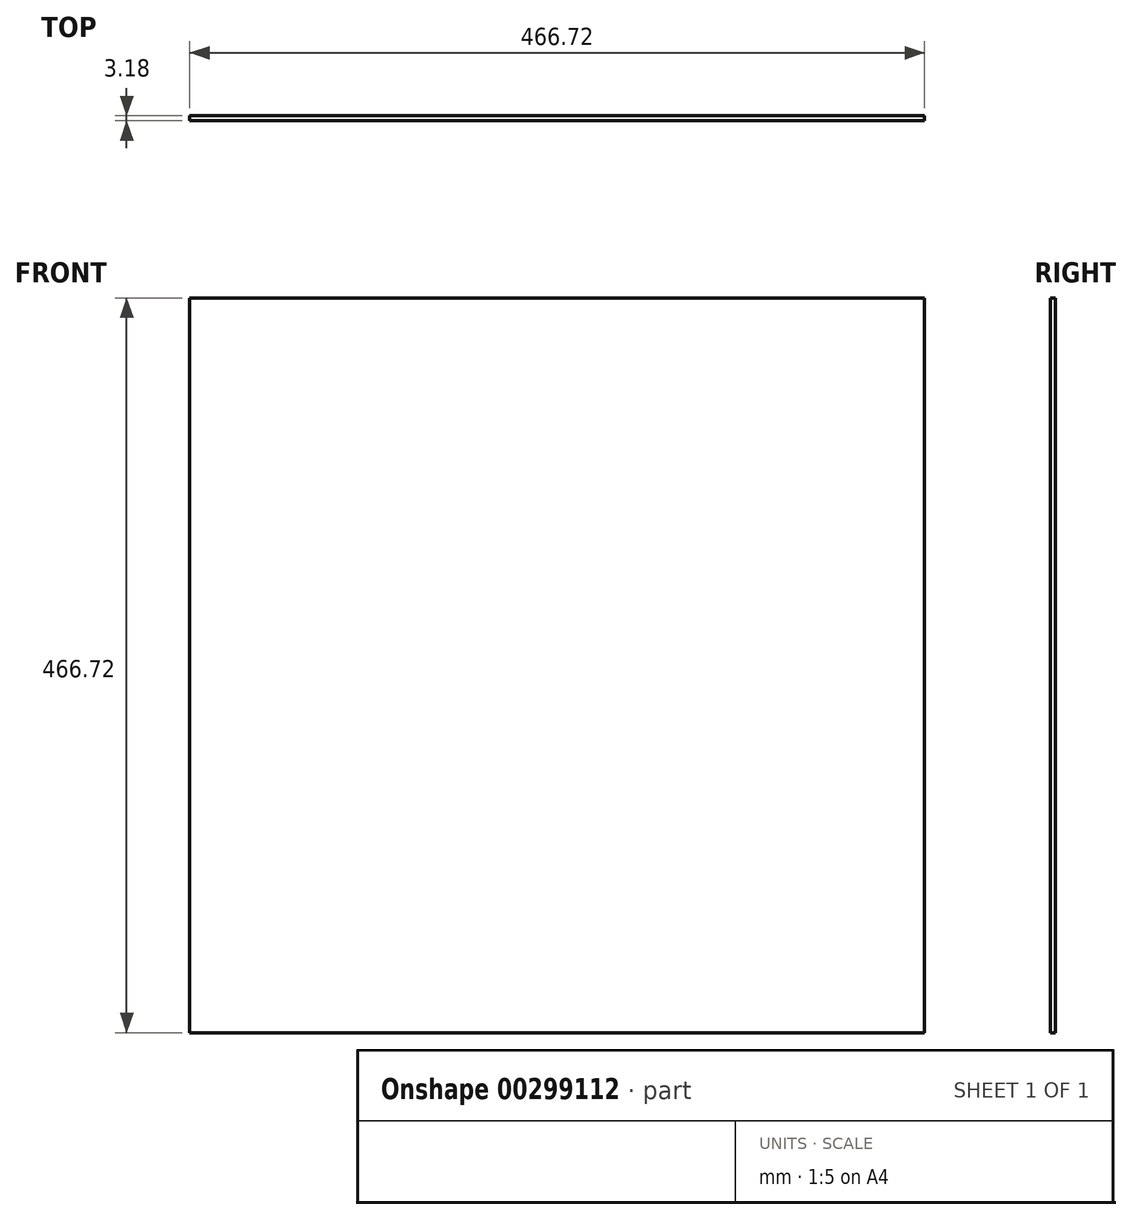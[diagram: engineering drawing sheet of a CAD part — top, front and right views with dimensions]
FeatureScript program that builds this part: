
annotation { "Feature Type Name" : "Feature", "Feature Type Description" : "" }
export const myFeature = defineFeature(function(context is Context, id is Id, definition is map)
    precondition{}
    {
        {
            var Q0;
            Q0=qCreatedBy(makeId("Front.planeOp"),FACE);
            var sketch = newSketch(context, id + "F0", { "sketchPlane" : qUnion([Q0])});
            skLineSegment(sketch, "E0.bottom", {"start": v(233.36, 233.36) * mm, "end": v(-233.36, 233.36) * mm});
            skLineSegment(sketch, "E0.top", {"start": v(233.36, -233.36) * mm, "end": v(-233.36, -233.36) * mm});
            skLineSegment(sketch, "E0.left", {"start": v(233.36, 233.36) * mm, "end": v(233.36, -233.36) * mm});
            skLineSegment(sketch, "E0.right", {"start": v(-233.36, 233.36) * mm, "end": v(-233.36, -233.36) * mm});
            skPoint(sketch, "E0.middle", {"position": v(0, 0) * mm});
            skSolve(sketch);
        }
        {
            var Q0;
            Q0 = qSketchRegion(id + "F0", true);
            extrude(context, id + "F1", {"entities" : qUnion([Q0]), "endBound" : BoundingType.SYMMETRIC, "depth" : 3.17 * mm});
        }
        {
            var Q0;
            Q0=makeQuery(id+"F1.opExtrude","CAP_FACE",FACE,{"disambiguationData":[OSD([sQuery(id+"F0.wireOp",EDGE,"E0.bottom"),sQuery(id+"F0.wireOp",EDGE,"E0.top"),sQuery(id+"F0.wireOp",EDGE,"E0.left"),sQuery(id+"F0.wireOp",EDGE,"E0.right")])],"isStart":false});
            var sketch = newSketch(context, id + "F2", { "sketchPlane" : qUnion([Q0])});
            skLineSegment(sketch, "E1.bottom", {"start": v(16.67, 16.67) * mm, "end": v(-16.67, 16.67) * mm, "construction": true});
            skLineSegment(sketch, "E1.top", {"start": v(16.67, -16.67) * mm, "end": v(-16.67, -16.67) * mm, "construction": true});
            skLineSegment(sketch, "E1.left", {"start": v(16.67, 16.67) * mm, "end": v(16.67, -16.67) * mm, "construction": true});
            skLineSegment(sketch, "E1.right", {"start": v(-16.67, 16.67) * mm, "end": v(-16.67, -16.67) * mm, "construction": true});
            skPoint(sketch, "E1.middle", {"position": v(0, 0) * mm});
            skLineSegment(sketch, "E2.bottom", {"start": v(-16.67, 16.67) * mm, "end": v(16.67, 16.67) * mm});
            skLineSegment(sketch, "E2.top", {"start": v(-16.67, -16.67) * mm, "end": v(16.67, -16.67) * mm});
            skLineSegment(sketch, "E2.left", {"start": v(-16.67, 16.67) * mm, "end": v(-16.67, -16.67) * mm});
            skLineSegment(sketch, "E2.right", {"start": v(16.67, 16.67) * mm, "end": v(16.67, -16.67) * mm});
            skLineSegment(sketch, "E3.bottom", {"start": v(16.67, 16.67) * mm, "end": v(19.84, 16.67) * mm});
            skLineSegment(sketch, "E3.top", {"start": v(16.67, -16.67) * mm, "end": v(19.84, -16.67) * mm});
            skLineSegment(sketch, "E3.right", {"start": v(19.84, 16.67) * mm, "end": v(19.84, -16.67) * mm});
            skLineSegment(sketch, "E4.bottom", {"start": v(-16.67, 16.67) * mm, "end": v(-19.84, 16.67) * mm});
            skLineSegment(sketch, "E4.top", {"start": v(-16.67, -16.67) * mm, "end": v(-19.84, -16.67) * mm});
            skLineSegment(sketch, "E4.right", {"start": v(-19.84, 16.67) * mm, "end": v(-19.84, -16.67) * mm});
            skSolve(sketch);
        }
    });
